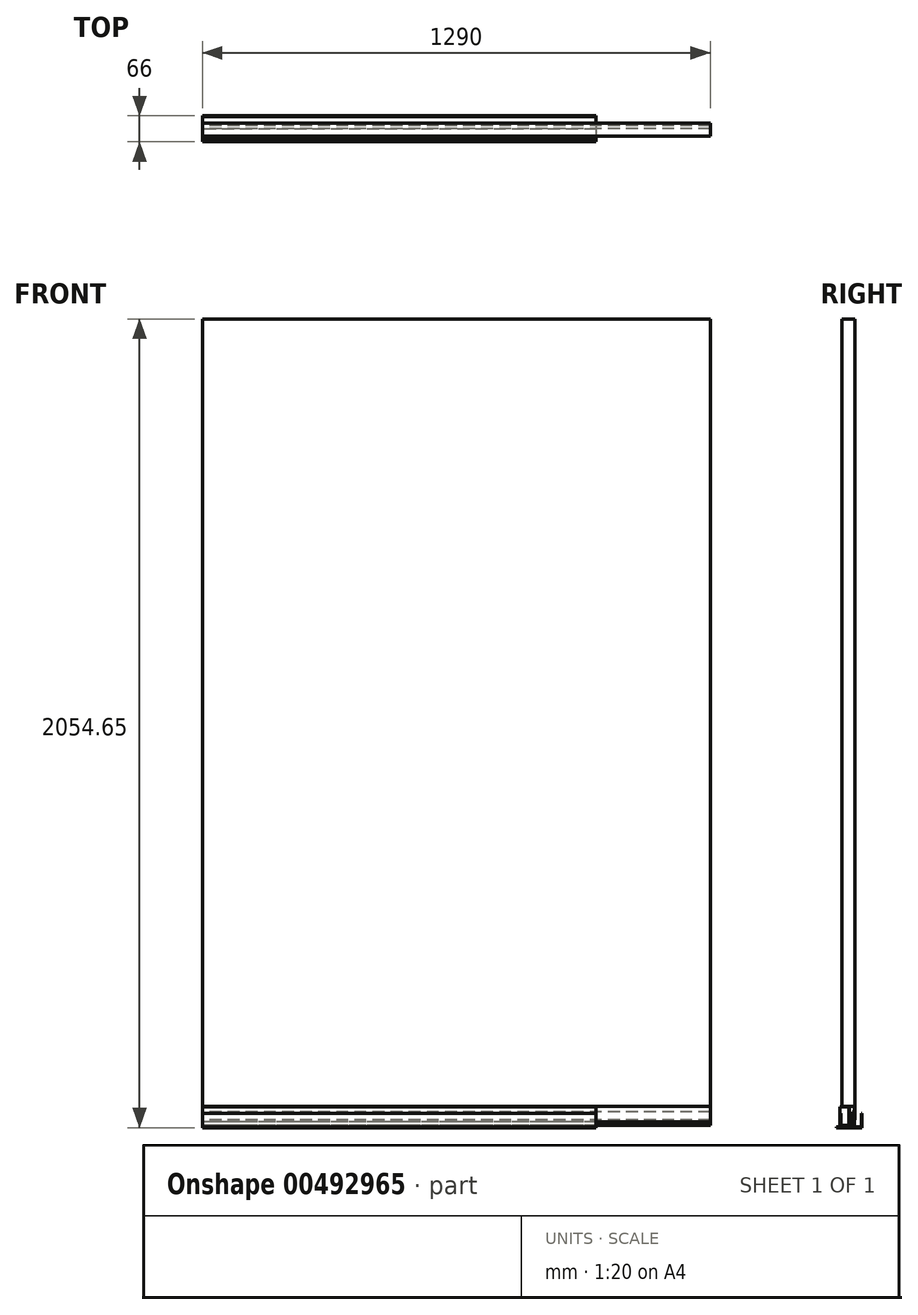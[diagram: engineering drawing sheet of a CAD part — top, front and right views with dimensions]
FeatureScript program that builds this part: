
annotation { "Feature Type Name" : "Feature", "Feature Type Description" : "" }
export const myFeature = defineFeature(function(context is Context, id is Id, definition is map)
    precondition{}
    {
        {
            var Q0;
            Q0=qCreatedBy(makeId("Right.planeOp"),FACE);
            var sketch = newSketch(context, id + "F0", { "sketchPlane" : qUnion([Q0])});
            skLineSegment(sketch, "E0", {"start": v(0, 0) * mm, "end": v(0, 36) * mm});
            skLineSegment(sketch, "E1", {"start": v(0, 0) * mm, "end": v(-66, 0) * mm});
            skLineSegment(sketch, "E2.0", {"start": v(-1.5, 1.5) * mm, "end": v(-56, 1.5) * mm});
            skLineSegment(sketch, "E2.1", {"start": v(-1.5, 1.5) * mm, "end": v(-1.5, 36) * mm});
            skLineSegment(sketch, "E3", {"start": v(0, 36) * mm, "end": v(-1.5, 36) * mm});
            skLineSegment(sketch, "E4", {"start": v(-66, 1.5) * mm, "end": v(-66, 0) * mm});
            skLineSegment(sketch, "E5", {"start": v(-20, 36.5) * mm, "end": v(-20, 1.5) * mm});
            skLineSegment(sketch, "E6", {"start": v(-56, 1.5) * mm, "end": v(-56, 36.5) * mm});
            skLineSegment(sketch, "E7", {"start": v(-20, 1.5) * mm, "end": v(-66, 1.5) * mm});
            skLineSegment(sketch, "E8.0", {"start": v(-54.5, 3) * mm, "end": v(-54.5, 36.5) * mm});
            skLineSegment(sketch, "E8.1", {"start": v(-21.5, 3) * mm, "end": v(-54.5, 3) * mm});
            skLineSegment(sketch, "E8.2", {"start": v(-21.5, 36.5) * mm, "end": v(-21.5, 3) * mm});
            skLineSegment(sketch, "E9", {"start": v(-20, 36.5) * mm, "end": v(-21.5, 36.5) * mm});
            skLineSegment(sketch, "E10", {"start": v(-54.5, 36.5) * mm, "end": v(-56, 36.5) * mm});
            skLineSegment(sketch, "E11.bottom", {"start": v(-18, 2054.65) * mm, "end": v(-51, 2054.65) * mm});
            skLineSegment(sketch, "E11.top", {"start": v(-18, 54.65) * mm, "end": v(-51, 54.65) * mm});
            skLineSegment(sketch, "E11.left", {"start": v(-18, 2054.65) * mm, "end": v(-18, 54.65) * mm});
            skLineSegment(sketch, "E11.right", {"start": v(-51, 2054.65) * mm, "end": v(-51, 54.65) * mm});
            skLineSegment(sketch, "E12.bottom", {"start": v(-34, 53) * mm, "end": v(-52.72, 53) * mm});
            skLineSegment(sketch, "E12.left", {"start": v(-34, 53) * mm, "end": v(-34, 6) * mm});
            skLineSegment(sketch, "E13", {"start": v(-34, 6) * mm, "end": v(-54.5, 6) * mm});
            skLineSegment(sketch, "E14", {"start": v(-18, 1.5) * mm, "end": v(-18, 3001.5) * mm, "construction": true});
            skLineSegment(sketch, "E15", {"start": v(-52.72, 53) * mm, "end": v(-56, 53) * mm});
            skLineSegment(sketch, "E16", {"start": v(-56, 53) * mm, "end": v(-56, 36.5) * mm});
            skLineSegment(sketch, "E17", {"start": v(-54.5, 36.5) * mm, "end": v(-54.5, 6) * mm});
            skLineSegment(sketch, "E18.left", {"start": v(-18, 54.65) * mm, "end": v(-18, 19.65) * mm});
            skLineSegment(sketch, "E19", {"start": v(-18, 19.65) * mm, "end": v(-19.5, 19.65) * mm});
            skLineSegment(sketch, "E20", {"start": v(-19.5, 19.65) * mm, "end": v(-19.5, 54.65) * mm});
            skLineSegment(sketch, "E21", {"start": v(-19.5, 40.25) * mm, "end": v(-23, 40.25) * mm});
            skLineSegment(sketch, "E22", {"start": v(-23, 40.25) * mm, "end": v(-23, 14.65) * mm});
            skLineSegment(sketch, "E23", {"start": v(-23, 14.65) * mm, "end": v(-32.5, 14.65) * mm});
            skLineSegment(sketch, "E24", {"start": v(-32.5, 14.65) * mm, "end": v(-32.5, 54.65) * mm});
            skLineSegment(sketch, "E25", {"start": v(-23, 40.25) * mm, "end": v(-23, 5.25) * mm});
            skLineSegment(sketch, "E26", {"start": v(-23, 5.25) * mm, "end": v(-24.5, 5.25) * mm});
            skLineSegment(sketch, "E27", {"start": v(-24.5, 5.25) * mm, "end": v(-24.5, 40.25) * mm});
            skLineSegment(sketch, "E28", {"start": v(-23, 40.25) * mm, "end": v(-24.5, 40.25) * mm});
            skLineSegment(sketch, "E29", {"start": v(-32.5, 54.65) * mm, "end": v(-32.5, 54.65) * mm});
            skLineSegment(sketch, "E30", {"start": v(-32.5, 54.65) * mm, "end": v(-18, 54.65) * mm});
            skPoint(sketch, "E31", {"position": v(-34.5, 54.65) * mm});
            skSolve(sketch);
        }
        {
            var Q0;
            {var subQ3=sQuery(id+"F0.wireOp",EDGE,"E18.left");Q0=makeQuery(id+"F0.imprint","IMPRINT",FACE,{"disambiguationData":[TD([[makeQuery(id+"F0.imprint","IMPRINT",EDGE,{"derivedFrom":subQ3}),-1.0]])]});}
            var Q1;
            {var subQ5=sQuery(id+"F0.wireOp",EDGE,"E26");Q1=makeQuery(id+"F0.imprint","IMPRINT",FACE,{"disambiguationData":[TD([[makeQuery(id+"F0.imprint","IMPRINT",EDGE,{"derivedFrom":subQ5}),-1.0]])]});}
            var Q2;
            {var subQ5=sQuery(id+"F0.wireOp",EDGE,"E28");Q2=makeQuery(id+"F0.imprint","IMPRINT",FACE,{"disambiguationData":[TD([[makeQuery(id+"F0.imprint","IMPRINT",EDGE,{"derivedFrom":subQ5}),1.0]])]});}
            extrude(context, id + "F1", {"entities" : qUnion([Q0, Q1, Q2]), "depth" : 1290 * mm});
        }
        {
            var Q0;
            {var subQ4=sQuery(id+"F0.wireOp",EDGE,"E21");Q0=makeQuery(id+"F0.imprint","IMPRINT",FACE,{"disambiguationData":[TD([[makeQuery(id+"F0.imprint","IMPRINT",EDGE,{"derivedFrom":subQ4}),-1.0]])]});}
            var Q1;
            Q1=makeQuery(id+"F1.opExtrude","CAP_FACE",FACE,{"disambiguationData":[OSD([sQuery(id+"F0.wireOp",EDGE,"E25"),sQuery(id+"F0.wireOp",EDGE,"E26"),sQuery(id+"F0.wireOp",EDGE,"E27"),sQuery(id+"F0.wireOp",EDGE,"E28")])],"isStart":false});
            extrude(context, id + "F2", {"entities" : qUnion([Q0]), "endBound" : BoundingType.UP_TO_SURFACE, "endBoundEntityFace" : qUnion([Q1]), "depth" : 25 * mm});
        }
        {
            var Q0;
            Q0=makeQuery(id+"F0.imprint","IMPRINT",FACE,{"disambiguationData":[TD([[makeQuery(id+"F0.imprint","IMPRINT",EDGE,{"derivedFrom":sQuery(id+"F0.wireOp",EDGE,"E0")}),1.0]])]});
            var Q1;
            Q1=makeQuery(id+"F0.imprint","IMPRINT",FACE,{"disambiguationData":[TD([[makeQuery(id+"F0.imprint","IMPRINT",EDGE,{"derivedFrom":sQuery(id+"F0.wireOp",EDGE,"E10")}),-1.0]])]});
            extrude(context, id + "F3", {"entities" : qUnion([Q0, Q1]), "depth" : 1000 * mm});
        }
        {
            var Q0;
            {var subQ1=sQuery(id+"F0.wireOp",EDGE,"E5");Q0=makeQuery(id+"F0.imprint","IMPRINT",FACE,{"disambiguationData":[TD([[makeQuery(id+"F0.imprint","IMPRINT",EDGE,{"derivedFrom":subQ1}),-1.0]])]});}
            var Q1;
            Q1=makeQuery(id+"F3.opExtrude","CAP_FACE",FACE,{"disambiguationData":[OSD([sQuery(id+"F0.wireOp",EDGE,"E0"),sQuery(id+"F0.wireOp",EDGE,"E1"),sQuery(id+"F0.wireOp",EDGE,"E2.0"),sQuery(id+"F0.wireOp",EDGE,"E2.1"),sQuery(id+"F0.wireOp",EDGE,"E3"),sQuery(id+"F0.wireOp",EDGE,"E4"),sQuery(id+"F0.wireOp",EDGE,"E7")])],"isStart":false});
            extrude(context, id + "F4", {"entities" : qUnion([Q0]), "endBoundEntityFace" : qUnion([Q1]), "depth" : 1000 * mm});
        }
        {
            var Q0;
            Q0=makeQuery(id+"F0.imprint","IMPRINT",FACE,{"disambiguationData":[TD([[makeQuery(id+"F0.imprint","IMPRINT",EDGE,{"derivedFrom":sQuery(id+"F0.wireOp",EDGE,"E11.bottom")}),1.0]])]});
            var Q1;
            Q1=makeQuery(id+"F2.opExtrude","CAP_FACE",FACE,{"disambiguationData":[OSD([sQuery(id+"F0.wireOp",EDGE,"E25"),sQuery(id+"F0.wireOp",EDGE,"E26"),sQuery(id+"F0.wireOp",EDGE,"E27"),sQuery(id+"F0.wireOp",EDGE,"E28")])],"isStart":false});
            extrude(context, id + "F5", {"entities" : qUnion([Q0]), "endBound" : BoundingType.UP_TO_SURFACE, "endBoundEntityFace" : qUnion([Q1]), "depth" : 25 * mm});
        }
    });
